FCSTD DOCUMENT  (FreeCAD 0.16R6710 (Git))
Label: working_sketch
License: All rights reserved
LicenseURL: http://en.wikipedia.org/wiki/All_rights_reserved
objects: Part::Feature×21, Part::Part2DObjectPython×10, Part::FeaturePython×2
note: 33 computed .brp shape members not serialized (recipe doc carries the construction recipe); baked Part::Feature solids carry a one-line shape summary decoded from their .brp

FEATURE [Part::Feature] Shape025
  Placement = pos=(13612.6,-39706.8,0) rot=(0,0,1;1.5708rad)
  shape: bbox 19.5 x 2e-07 x 2e-07 mm, 0 faces, 0 solids (baked)
FEATURE [Part::Feature] Shape026
  Placement = pos=(13612.6,-39706.8,0) rot=(0,0,1;1.5708rad)
  shape: bbox 2e-07 x 293.2 x 2e-07 mm, 0 faces, 0 solids (baked)
FEATURE [Part::Feature] Shape027
  Placement = pos=(13612.6,-39706.8,0) rot=(0,0,1;1.5708rad)
  shape: bbox 19.5 x 2e-07 x 2e-07 mm, 0 faces, 0 solids (baked)
FEATURE [Part::Feature] Shape028
  Placement = pos=(13612.6,-39706.8,0) rot=(0,0,1;1.5708rad)
  shape: bbox 60 x 38.1 x 2e-07 mm, 0 faces, 0 solids (baked)
FEATURE [Part::Feature] Shape029
  Placement = pos=(13612.6,-39706.8,0) rot=(0,0,1;1.5708rad)
  shape: bbox 7 x 2e-07 x 2e-07 mm, 0 faces, 0 solids (baked)
FEATURE [Part::Feature] Shape030
  Placement = pos=(13612.6,-39706.8,0) rot=(0,0,1;1.5708rad)
  shape: bbox 2e-07 x 216 x 2e-07 mm, 0 faces, 0 solids (baked)
FEATURE [Part::Feature] Shape031
  Placement = pos=(13612.6,-39706.8,0) rot=(0,0,1;1.5708rad)
  shape: bbox 7 x 2e-07 x 2e-07 mm, 0 faces, 0 solids (baked)
FEATURE [Part::Feature] Shape032
  Placement = pos=(13612.6,-39706.8,0) rot=(0,0,1;1.5708rad)
  shape: bbox 60 x 39.08 x 2e-07 mm, 0 faces, 0 solids (baked)
FEATURE [Part::Feature] Shape033
  Placement = pos=(13612.6,-39706.8,0) rot=(0,0,1;1.5708rad)
  shape: bbox 2e-07 x 293 x 2e-07 mm, 0 faces, 0 solids (baked)
FEATURE [Part::Feature] Shape034
  Placement = pos=(13612.6,-39706.8,0) rot=(0,0,1;1.5708rad)
  shape: bbox 12.22 x 67.21 x 2e-07 mm, 0 faces, 0 solids (baked)
FEATURE [Part::Feature] Shape035
  Placement = pos=(13612.6,-39706.8,0) rot=(0,0,1;1.5708rad)
  shape: bbox 2.428 x 111.8 x 2e-07 mm, 0 faces, 0 solids (baked)
FEATURE [Part::Feature] Shape036
  Placement = pos=(13612.6,-39706.8,0) rot=(0,0,1;1.5708rad)
  shape: bbox 9.79 x 37.02 x 2e-07 mm, 0 faces, 0 solids (baked)
FEATURE [Part::Feature] Shape037
  Placement = pos=(13612.6,-39706.8,0) rot=(0,0,1;1.5708rad)
  shape: bbox 9.217 x 57.37 x 2e-07 mm, 0 faces, 0 solids (baked)
FEATURE [Part::Feature] Shape038
  Placement = pos=(13612.6,-39706.8,0) rot=(0,0,1;1.5708rad)
  shape: bbox 2.422 x 111.5 x 2e-07 mm, 0 faces, 0 solids (baked)
FEATURE [Part::Feature] Shape039
  Placement = pos=(13612.6,-39706.8,0) rot=(0,0,1;1.5708rad)
  shape: bbox 6.794 x 28.96 x 2e-07 mm, 0 faces, 0 solids (baked)
FEATURE [Part::Feature] Shape040
  Placement = pos=(13612.6,-39706.8,0) rot=(0,0,1;1.5708rad)
  shape: bbox 29.08 x 80.8 x 2e-07 mm, 0 faces, 0 solids (baked)
FEATURE [Part::Feature] Shape041
  Placement = pos=(13612.6,-39706.8,0) rot=(0,0,1;1.5708rad)
  shape: bbox 3.099 x 172.2 x 2e-07 mm, 0 faces, 0 solids (baked)
FEATURE [Part::Feature] Shape042
  Placement = pos=(13612.6,-39706.8,0) rot=(0,0,1;1.5708rad)
  shape: bbox 21.74 x 40.17 x 2e-07 mm, 0 faces, 0 solids (baked)
FEATURE [Part::Feature] Shape043
  Placement = pos=(13612.6,-39706.8,0) rot=(0,0,1;1.5708rad)
  shape: bbox 27.08 x 76.53 x 2e-07 mm, 0 faces, 0 solids (baked)
FEATURE [Part::Feature] Shape044
  Placement = pos=(13612.6,-39706.8,0) rot=(0,0,1;1.5708rad)
  shape: bbox 3.097 x 172.1 x 2e-07 mm, 0 faces, 0 solids (baked)
FEATURE [Part::Feature] Shape045
  Placement = pos=(13612.6,-39706.8,0) rot=(0,0,1;1.5708rad)
  shape: bbox 23.98 x 38.93 x 2e-07 mm, 0 faces, 0 solids (baked)
FEATURE [Part::Part2DObjectPython] Line  # Draft 2D object (typed FeaturePython)
  ChamferSize = 0
  Closed = false
  End = (-3.7991e-08,39.0772,0)
  FilletRadius = 0
  Length = 216
  MakeFace = true
  Placement = pos=(13612.6,-39706.8,0) rot=(0,0,1;1.5708rad)
  Points = (2) [(39961.9,13612.6,0),(39745.9,13612.6,0)]
  Start = (-3.7991e-08,255.077,0)
  Subdivisions = 0
FEATURE [Part::Part2DObjectPython] Line001  # Draft 2D object (typed FeaturePython)
  ChamferSize = 0
  Closed = false
  End = (81.5,293.177,0)
  FilletRadius = 0
  Length = 293.177
  MakeFace = true
  Placement = pos=(13599,-39667.1,0) rot=(0,0,1;1.5708rad)
  Points = (2) [(39667.1,13517.5,0),(39960.3,13517.5,0)]
  Start = (81.5,-1.7302e-08,0)
  Subdivisions = 0
FEATURE [Part::Part2DObjectPython] DWire  # Draft 2D object (typed FeaturePython)
  ChamferSize = 0
  Closed = false
  End = (-0.0288554,249.942,0)
  FilletRadius = 0
  Length = 204.893
  MakeFace = true
  Placement = pos=(13599,-39667.1,0) rot=(0,0,1;1.5708rad)
  Points = (17) [(39714.2,13598.6,0),(39723.9,13595.7,0),(39738.1,13592.6,0),(39753.3,13590.3,0),(39765.7,13589.3,0),(39773.4,13588.8,0),(39789.7,13589.1,0),+10 more]
  Start = (0.42427,47.0706,0)
  Subdivisions = 0
FEATURE [Part::Part2DObjectPython] DWire001  # Draft 2D object (typed FeaturePython)
  ChamferSize = 0
  Closed = false
  End = (0.271926,244.207,0)
  FilletRadius = 0
  Length = 193.736
  MakeFace = true
  Placement = pos=(13599,-39667.1,0) rot=(0,0,1;1.5708rad)
  Points = (14) [(39719.1,13598.7,0),(39726.3,13596.7,0),(39739.6,13593.7,0),(39754.7,13592,0),(39771,13590.7,0),(39785.5,13590.7,0),(39806.7,13591.3,0),+7 more]
  Start = (0.345168,51.9417,0)
  Subdivisions = 0
FEATURE [Part::Part2DObjectPython] DWire002  # Draft 2D object (typed FeaturePython)
  ChamferSize = 0
  Closed = false
  End = (80.768,292.383,0)
  FilletRadius = 0
  Length = 302.789
  MakeFace = true
  Placement = pos=(13599,-39667.1,0) rot=(0,0,1;1.5708rad)
  Points = (20) [(39671,13517.5,0),(39677.9,13522.9,0),(39689.1,13529.1,0),(39701.5,13535.6,0),(39717.7,13541,0),(39733.8,13543.9,0),(39746.8,13544.7,0),+13 more]
  Start = (81.4614,3.92221,0)
  Subdivisions = 0
FEATURE [Part::Part2DObjectPython] Line002  # Draft 2D object (typed FeaturePython)
  ChamferSize = 0
  Closed = false
  End = (9e-12,-41.4294,0)
  FilletRadius = 0
  Length = 80.5065
  MakeFace = true
  Placement = pos=(13599,-39667.1,0) rot=(0,0,1;1.5708rad)
  Points = (2) [(39706.2,13599,0),(39625.7,13599,0)]
  Start = (9e-12,39.0772,0)
  Subdivisions = 0
FEATURE [Part::Part2DObjectPython] Line003  # Draft 2D object (typed FeaturePython)
  ChamferSize = 0
  Closed = false
  End = (9e-12,0,0)
  FilletRadius = 0
  Length = 64.5
  MakeFace = true
  Placement = pos=(13599,-39667.1,0) rot=(0,0,1;1.5708rad)
  Points = (2) [(39667.1,13534.5,0),(39667.1,13599,0)]
  Start = (64.5,0,0)
  Subdivisions = 0
FEATURE [Part::FeaturePython] Point  # WARN: FeaturePython — macro-defined, semantics opaque (R4)
  X = 0
  Y = 0
  Z = 0
FEATURE [Part::FeaturePython] Scale  # Draft clone (typed FeaturePython)
  Objects = -> [Shape027,Shape025,Shape026,Shape028,Shape029,Shape030,Shape031,Shape032,Shape033,Shape034,Shape035,Shape036,Shape037,Shape038,Shape039,Shape040,Shape041,Shape042,Shape043,Shape044,Shape045,Line,Line001,DWire,DWire001,DWire002,Line002,Line003,Point]
  Placement = pos=(-8e-12,0,0) rot=(0,0,1;0rad)
  Scale = (0.1,0.1,1)
FEATURE [Part::Part2DObjectPython] DWire003  # Draft 2D object (typed FeaturePython)
  ChamferSize = 0
  Closed = true
  End = (-0.00809709,6.39837,0)
  FilletRadius = 0
  Length = 40.9618
  MakeFace = true
  Points = (16) [(0.00470631,4.6626,0),(0.637861,7.10972,0),(1.02176,10.6289,0),(1.02176,10.6289,0),(0.778971,21.8052,0),(0.587126,22.9024,0),(0.350229,23.9212,0),+9 more]
  Start = (0.00470631,4.6626,0)
  Subdivisions = 0
FEATURE [Part::Part2DObjectPython] DWire004  # Draft 2D object (typed FeaturePython)
  ChamferSize = 0
  Closed = true
  End = (8.4,-1.733e-09,0)
  FilletRadius = 0
  Length = 62.4483
  MakeFace = true
  Points = (27) [(8.11436,-1.73313e-09,0),(6.76597,2.0229,0),(5.78177,4.37147,0),(5.34317,6.25104,0),(5.2482,7.40167,0),(5.19219,8.08026,0),(5.38901,19.0179,0),+20 more]
  Start = (8.11436,-1.733e-09,0)
  Subdivisions = 0
FEATURE [Part::Part2DObjectPython] DWire005  # Draft 2D object (typed FeaturePython)
  ChamferSize = 0
  Closed = true
  End = (-0.25,3.90772,0)
  FilletRadius = 0
  Length = 70.5985
  MakeFace = true
  Points = (24) [(-3.80714e-09,4.59544,0),(0.677704,6.94232,0),(1.08143,10.595,0),(0.939799,18.0688,0),(0.866146,21.8363,0),(0.559057,23.4751,0),(0.202211,24.6477,0),+17 more]
  Start = (-3.807e-09,4.59544,0)
  Subdivisions = 0
